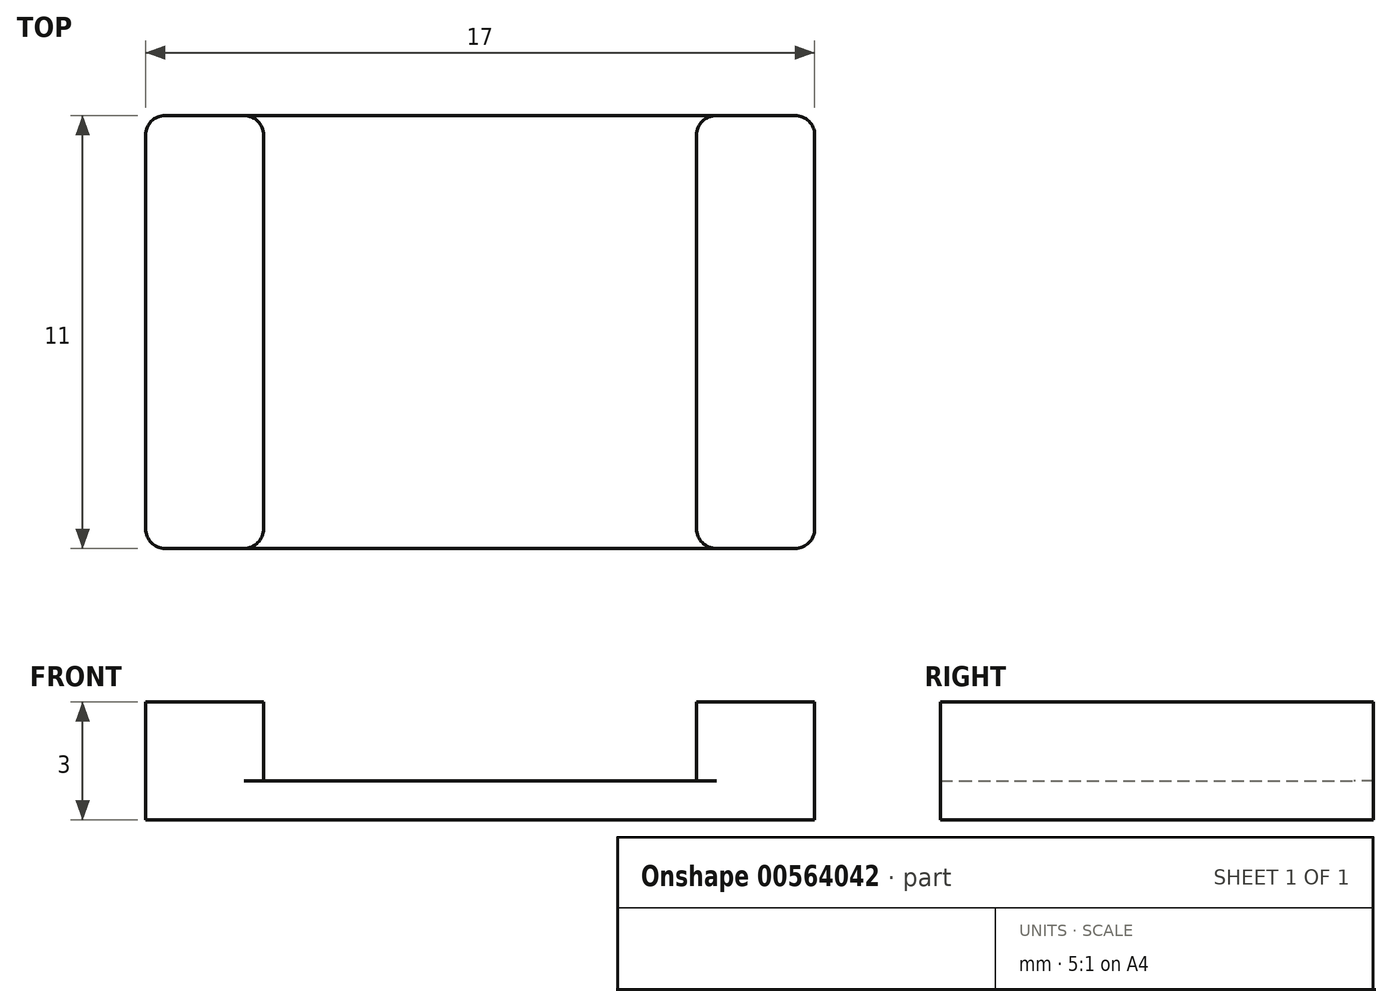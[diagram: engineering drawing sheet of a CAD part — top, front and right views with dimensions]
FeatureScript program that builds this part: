
annotation { "Feature Type Name" : "Feature", "Feature Type Description" : "" }
export const myFeature = defineFeature(function(context is Context, id is Id, definition is map)
    precondition{}
    {
        {
            var Q0;
            Q0=qCreatedBy(makeId("Top.planeOp"),FACE);
            var sketch = newSketch(context, id + "F0", { "sketchPlane" : qUnion([Q0])});
            skLineSegment(sketch, "E0.bottom", {"start": v(5.5, -5.5) * mm, "end": v(-5.5, -5.5) * mm});
            skLineSegment(sketch, "E0.top", {"start": v(5.5, 5.5) * mm, "end": v(-5.5, 5.5) * mm});
            skLineSegment(sketch, "E0.left", {"start": v(5.5, -5.5) * mm, "end": v(5.5, 5.5) * mm});
            skLineSegment(sketch, "E0.right", {"start": v(-5.5, -5.5) * mm, "end": v(-5.5, 5.5) * mm});
            skPoint(sketch, "E0.middle", {"position": v(0, 0) * mm});
            skLineSegment(sketch, "E1.bottom", {"start": v(-5.5, 5.5) * mm, "end": v(-8.5, 5.5) * mm});
            skLineSegment(sketch, "E1.top", {"start": v(-5.5, -5.5) * mm, "end": v(-8.5, -5.5) * mm});
            skLineSegment(sketch, "E1.left", {"start": v(-5.5, 5.5) * mm, "end": v(-5.5, -5.5) * mm});
            skLineSegment(sketch, "E1.right", {"start": v(-8.5, 5.5) * mm, "end": v(-8.5, -5.5) * mm});
            skLineSegment(sketch, "E2.bottom", {"start": v(5.5, 5.5) * mm, "end": v(8.5, 5.5) * mm});
            skLineSegment(sketch, "E2.top", {"start": v(5.5, -5.5) * mm, "end": v(8.5, -5.5) * mm});
            skLineSegment(sketch, "E2.left", {"start": v(5.5, 5.5) * mm, "end": v(5.5, -5.5) * mm});
            skLineSegment(sketch, "E2.right", {"start": v(8.5, 5.5) * mm, "end": v(8.5, -5.5) * mm});
            skSolve(sketch);
        }
        {
            var Q0;
            Q0=makeQuery(id+"F0.imprint","IMPRINT",FACE,{"disambiguationData":[TD([[makeQuery(id+"F0.imprint","IMPRINT",EDGE,{"derivedFrom":sQuery(id+"F0.wireOp",EDGE,"E1.bottom")}),1.0]])]});
            var Q1;
            Q1=makeQuery(id+"F0.imprint","IMPRINT",FACE,{"disambiguationData":[TD([[makeQuery(id+"F0.imprint","IMPRINT",EDGE,{"derivedFrom":sQuery(id+"F0.wireOp",EDGE,"E2.bottom")}),-1.0]])]});
            extrude(context, id + "F1", {"entities" : qUnion([Q0, Q1]), "depth" : 3 * mm, "offsetDistance" : 25 * mm});
        }
        {
            var Q0;
            Q0=makeQuery(id+"F0.imprint","IMPRINT",FACE,{"disambiguationData":[TD([[makeQuery(id+"F0.imprint","IMPRINT",EDGE,{"derivedFrom":sQuery(id+"F0.wireOp",EDGE,"E0.bottom")}),-1.0]])]});
            extrude(context, id + "F2", {"entities" : qUnion([Q0]), "operationType" : NewBodyOperationType.ADD, "depth" : 1 * mm, "offsetDistance" : 25 * mm});
        }
        {
            var Q0;
            Q0=makeQuery(id+"F1.opExtrude","SWEPT_EDGE",EDGE,{"disambiguationData":[OSD([sQuery(id+"F0.wireOp",EDGE,"E0.bottom"),sQuery(id+"F0.wireOp",EDGE,"E1.top"),sQuery(id+"F0.wireOp",EDGE,"E1.left")])]});
            var Q1;
            Q1=makeQuery(id+"F1.opExtrude","SWEPT_EDGE",EDGE,{"disambiguationData":[OSD([sQuery(id+"F0.wireOp",EDGE,"E0.bottom"),sQuery(id+"F0.wireOp",EDGE,"E2.top"),sQuery(id+"F0.wireOp",EDGE,"E2.left")])]});
            var Q2;
            Q2=makeQuery(id+"F1.opExtrude","SWEPT_EDGE",EDGE,{"disambiguationData":[OSD([sQuery(id+"F0.wireOp",EDGE,"E2.top"),sQuery(id+"F0.wireOp",EDGE,"E2.right")])]});
            var Q3;
            Q3=makeQuery(id+"F1.opExtrude","SWEPT_EDGE",EDGE,{"disambiguationData":[OSD([sQuery(id+"F0.wireOp",EDGE,"E2.bottom"),sQuery(id+"F0.wireOp",EDGE,"E2.right")])]});
            var Q4;
            Q4=makeQuery(id+"F1.opExtrude","SWEPT_EDGE",EDGE,{"disambiguationData":[OSD([sQuery(id+"F0.wireOp",EDGE,"E1.top"),sQuery(id+"F0.wireOp",EDGE,"E1.right")])]});
            var Q5;
            Q5=makeQuery(id+"F1.opExtrude","SWEPT_EDGE",EDGE,{"disambiguationData":[OSD([sQuery(id+"F0.wireOp",EDGE,"E0.top"),sQuery(id+"F0.wireOp",EDGE,"E1.bottom"),sQuery(id+"F0.wireOp",EDGE,"E1.left")])]});
            var Q6;
            Q6=makeQuery(id+"F1.opExtrude","SWEPT_EDGE",EDGE,{"disambiguationData":[OSD([sQuery(id+"F0.wireOp",EDGE,"E1.bottom"),sQuery(id+"F0.wireOp",EDGE,"E1.right")])]});
            var Q7;
            Q7=makeQuery(id+"F1.opExtrude","SWEPT_EDGE",EDGE,{"disambiguationData":[OSD([sQuery(id+"F0.wireOp",EDGE,"E0.top"),sQuery(id+"F0.wireOp",EDGE,"E2.bottom"),sQuery(id+"F0.wireOp",EDGE,"E2.left")])]});
            fillet(context, id + "F3", {"entities" : qUnion([Q0, Q1, Q2, Q3, Q4, Q5, Q6, Q7]), "radius" : 0.5 * mm, "tangentPropagation" : true, "allowEdgeOverflow" : false});
        }
    });
